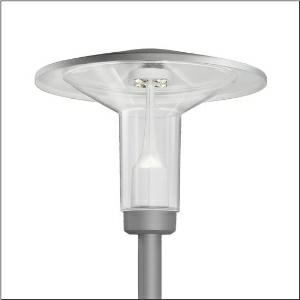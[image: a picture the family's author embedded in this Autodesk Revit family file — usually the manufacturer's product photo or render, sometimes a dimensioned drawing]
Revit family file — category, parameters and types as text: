
# Revit family: laterne_iq___p1_0a_5xa5255ff14h000022_5805
name_source: partatom
category: Lighting Fixtures
units: mm (PartAtom-declared; Revit-internal decimal feet)

## family parameters
Cut with Voids When Loaded = No
Host = Face
Light Source = No
Part Type = Normal
Room Calculation Point = No
Round Connector Dimension = Use Diameter
Shared = No

## types (1)
- --- (1 x LED, 1510 lm, 10.5 W, 3000K)
    Apparent Load = 11 VA
    CIE Flux Codes = 35 64 91 96 100
    Color Rendering = 70
    Color Temperature = 3000K
    Default Elevation = 1800 mm
    Description = Lantern iQ, mast luminaire, Module 540 iQ-SR, primary light control with 3 zone facetted reflector, of plastic, silver coated, highly specular, structured, primary optical cover: cover, of PMMA, transparent, light distribution: P1.0a, light emission: direct distribution, primary light characteristic: strongly asymmetric, installation type: post-top, LED, High Power LED, rated luminous flux: 1.510lm, luminous efficacy: 144lm/W, light colour: 730, colour temperature: 3000K, control gear: iQ Street-Remote, control: Street-Remote, Auto-Match, Temp-Guard, Lumen-Switch, Night-Set, Smart-Wire, Light-Fading, Desk-Remote (wireless, voltage-free reading and setting of iQ features in the workshop via application-optimized NFC function/RFID function), optimised constant luminous flux control (CLO 2.0), pre-setting: logarithmic dimming characteristic, mains connection: 230..240V, AC, 50/60Hz, connection cable pre-assembled, cable length: 5,5m, wiring characteristics: H07RN-F, start of lifetime: 11W, end of service life: 11W, reduction: 5W, luminaire housing, upper part, of glass-fibre reinforced polyester, coated, Siteco® metallic grey (DB 702S), diameter: 750mm, height: 583mm, spigot size: d x l = 76 x 70mm (post-top) | with reducer (optional accessory) 60 x 70mm, mounting height: 3..5m, post-top mast mounting element, of diecast aluminium, coated, Siteco® metallic grey (DB 702S), Module 540 iQ-SR, traffic white (RAL 9016), equipment: standard, protection rating (complete): IP65, insulation class (complete): insulation class II (safety insulation), certification: CE, ENEC, VDE, packaging unit: 1 piece

Light Distribution: P1.0a
    Height = 583 mm
    Lamp = 1 x LED
    Lamp Light Flux = 1510 lm
    Lamp Power = 10.5 W
    Lamp count = 1
    Length = 750 mm
    Luminous efficacy = 144 lm/W
    Manufacturer = Siteco
    ModVariant = No
    Model = 5XA5255FF14H000022
    Number of Poles = 1
    OnlyDefault = Yes
    Power Factor = 1
    Product Name = Laterne iQ | P1.0a
    Product group = mast luminaire | pylon top
    ProductGroupID = 6100
    Protection Class = Protection class II
    Protection Degree = IP 65
    RLX_Detail_Level = 1
    RLX_Emergency_Light_Flux = 0 lm
    RLX_Emergency_Type = 0
    RLX_Emergency_Type_DB = No
    RlxData = <blob elided: 33637 chars, md5=d650b5cb>
    Socket = socket
    Standby Power = 0 W
    System Light Flux = 1510 lm
    System Power = 11 W
    Type Comments = factory setting: luminous flux: 100 % | dim-lin: 254 | 419 mA
    Type Image = l_1006050.jpg
    URL = http://relux.com
    VarID = @adj_160466
    Voltage = 0 V
    Weight = 0.00 kg
    Width = 0 mm  [stored 0 ft]

note: [stored X ft] marks values corroborated as IEEE doubles in the binary element streams (Revit-internal decimal feet)

## geometry (parser evidence)
native form markers: Blend x4, Sweep x10
no freeform markers — native parametric forms only
